# Revit family: Toilet-Floor_Mount_Intelligent-KOHLER-Leap-K-29149-1
name_source: partatom
category: Plumbing Fixtures
units: mm (PartAtom-declared; Revit-internal decimal feet)

## family parameters
Cut with Voids When Loaded = No
Host = Face
Maintain Annotation Orientation = No
OmniClass Number = 23.31.19.00
Part Type = Normal
Room Calculation Point = No
Round Connector Dimension = Use Diameter
Shared = No

## types (1)
- 0-White
    ADA Compliant = Yes
    Apparent Load = 1800 VA
    Assembly Code = D2010100
    Bowl Height = 17"
    CW Connection = Yes
    Cold Water Inlet = Cold Water Inlet
    Date Modified = 12/02/2025
    Default Elevation = 0"
    Description = One-piece elongated smart toilet, dual-flush
    Electrical Connector = Yes
    Electrical Note = One Dedicated Circuit Required
    Finish = Kohler-Vitreous_China-0-White
    Flow Rate = 0 GPM
    Flush Rate- GPF = 1.28 GPF
    Flush Rate- LPF = 4.8 LPF
    HW Connection = No
    Height = 20 1/16"
    Hot Water Inlet = Hot Water Inlet
    Length = 26 13/16"
    Manufacturer = Kohler Co.
    Master Format 2014 = 22 42 13.13
    Master Format 2014 Name = Residential Water Closets
    Material = Vitreous China
    Model = K-29149-0
    Pressure = 0.00 psi
    Product Documentation Link = https://www.us.kohler.com
    Product Name = Leap
    Product Page URL = http://www.us.kohler.com
    Rough-In = 12"
    Seat Included = No
    Type = 1
    URL = http://www.us.kohler.com
    Vent Connection = No
    Voltage = 120 V
    Waste Connection = Yes
    Waste Water Outlet = Waste Water Outlet
    WaterSense Certified = Yes
    Width = 14 9/16"

## geometry (parser evidence)
native form markers: Sweep x4
no freeform markers — native parametric forms only
